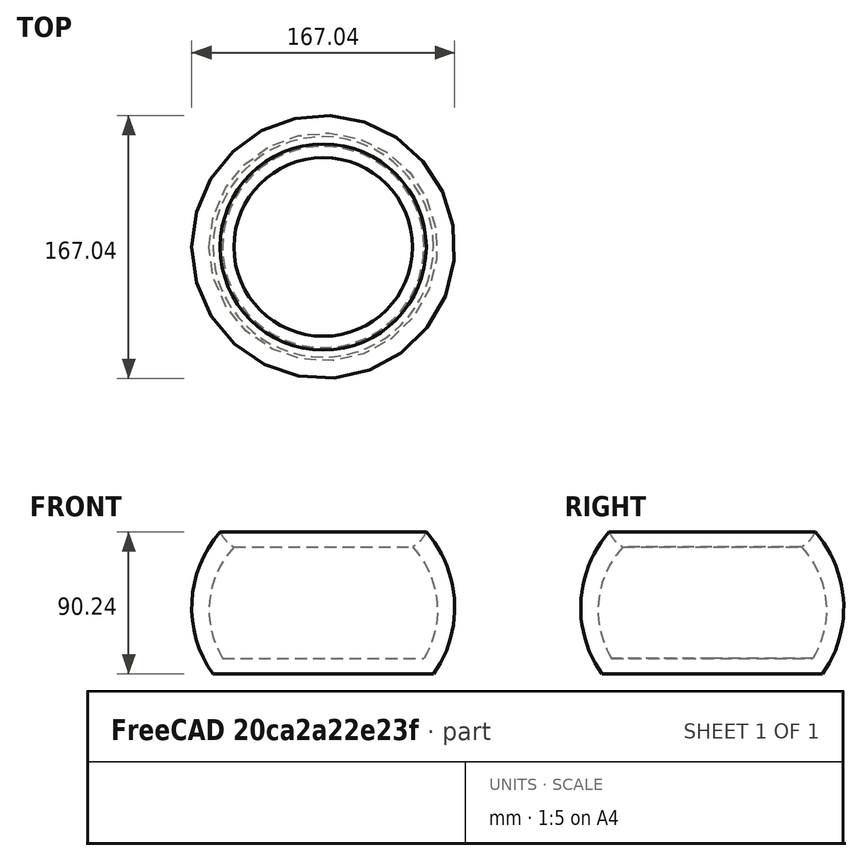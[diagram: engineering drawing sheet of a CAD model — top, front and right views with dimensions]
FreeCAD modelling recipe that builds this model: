
FCSTD DOCUMENT  (FreeCAD 0.17R13541 (Git))
Label: body
License: All rights reserved
LicenseURL: http://en.wikipedia.org/wiki/All_rights_reserved
objects: Sketcher::SketchObject×2, PartDesign::Revolution×1, PartDesign::Body×1
note: 5 computed .brp shape members not serialized (recipe doc carries the construction recipe); baked Part::Feature solids carry a one-line shape summary decoded from their .brp

FEATURE [Sketcher::SketchObject] Sketch
  MapMode = 5
  Placement = pos=(0,0,0) rot=(1,0,0;1.5708rad)
  Support = -> [XZ_Plane001]
  sketch-geometry (6):
    g0: LineSegment StartX=0 StartY=0 StartZ=0 EndX=-70 EndY=0 EndZ=0
    g1: ArcOfCircle CenterX=-10.7711 CenterY=42.2437 CenterZ=0 NormalX=0 NormalY=0 NormalZ=1 AngleXU=0 Radius=72.7501 StartAngle=2.42109 EndAngle=3.76114
    g2: ArcOfCircle CenterX=-47.1681 CenterY=98.1802 CenterZ=0 NormalX=0 NormalY=0 NormalZ=1 AngleXU=0 Radius=19.9228 StartAngle=3.55144 EndAngle=4.21328
    g3: ArcOfCircle CenterX=-13.5636 CenterY=40.5658 CenterZ=0 NormalX=0 NormalY=0 NormalZ=1 AngleXU=0 Radius=58.9141 StartAngle=2.39243 EndAngle=3.68706
    g4: LineSegment StartX=0 StartY=0 StartZ=0 EndX=0 EndY=10 EndZ=0
    g5: LineSegment StartX=0 StartY=10 StartZ=0 EndX=-63.9283 EndY=10 EndZ=0
  constraints (12):
    c: Coincident(g0,g-1)
    c: Horizontal(g0)
    c: Distance(g0) = 70
    c: Coincident(g1,g0)
    c: Coincident(g2,g1)
    c: Coincident(g3,g2)
    c: Coincident(g4,g-1)
    c: Vertical(g4)
    c: Distance(g4) = 10
    c: Coincident(g5,g4)
    c: Horizontal(g5)
    c: Coincident(g3,g5)
FEATURE [PartDesign::Revolution] Revolution
  Angle = 360
  Axis = (0,0,1)
  Base = (0,0,0)
  Placement = pos=(0,0,0) rot=(1,0,0;1.5708rad)
  Profile = -> Sketch
  ReferenceAxis = -> Sketch [V_Axis]
FEATURE [Sketcher::SketchObject] Sketch001
  MapMode = 5
  Placement = pos=(0,0,0) rot=(1,0,0;1.5708rad)
  Support = -> [XZ_Plane001]
  sketch-geometry (5):
    g0: Ellipse CenterX=-18.955 CenterY=55.4215 CenterZ=0 NormalX=0 NormalY=0 NormalZ=1 MajorRadius=22.5 MinorRadius=12.5 AngleXU=-1.5708
    g1: LineSegment [constr] StartX=-18.955 StartY=32.9215 StartZ=0 EndX=-18.955 EndY=77.9215 EndZ=0
    g2: LineSegment [constr] StartX=-6.45502 StartY=55.4215 StartZ=0 EndX=-31.455 EndY=55.4215 EndZ=0
    g3: GeomPoint X=-18.955 Y=36.7132 Z=0
    g4: GeomPoint X=-18.955 Y=74.1297 Z=0
  constraints (4):
    c: InternalAlignment(g1-g4 -> g0) x4
    c: Distance(g1) = 45
    c: Distance(g2) = 25
    c: Horizontal(g2)
FEATURE [PartDesign::Body] Body
  Group = -> [Sketch,Revolution,Sketch001]
  Origin = -> Origin001
  Tip = -> Revolution
